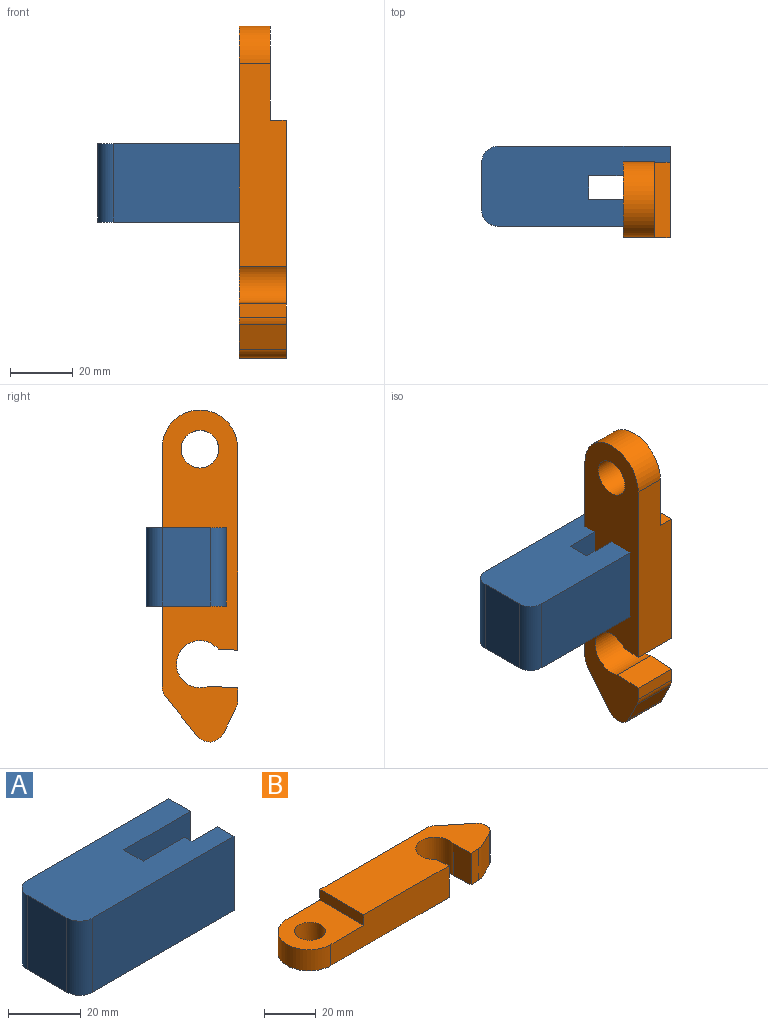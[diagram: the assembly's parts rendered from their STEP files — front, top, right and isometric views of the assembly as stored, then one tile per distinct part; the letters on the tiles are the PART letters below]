
ASSEMBLY  parts=2 mates=1
PART A: 14 faces, bbox 60x25.4x25 mm
  f0: plane 25x8.5mm, normal (1,0,0), area 212.5mm2, adj f1,f7,f8,f9
  f1: plane 55x25mm, normal (0,1,0), area 1375mm2, adj f0,f2,f7,f8
  f2: cylinder r=5mm len=25mm, axis (0,0,-1), area 196.3mm2, adj f1,f3,f7,f8
  f3: plane 25x15.4mm, normal (-1,0,0), area 385mm2, adj f2,f4,f7,f8
  f4: cylinder r=5mm len=25mm, axis (0,0,-1), area 196.3mm2, adj f3,f5,f7,f8
  f5: plane 55x25mm, normal (0,-1,0), area 1375mm2, adj f4,f6,f7,f8
  f6: plane 25x6.5mm, normal (1,0,0), area 162.5mm2, adj f5,f7,f8,f13
  f7: plane 60x25.4mm, normal (0,0,1), area 1289.1mm2, adj f0,f1,f2,f3,f4,f5,f6,f9
  f8: plane 60x25.4mm, normal (0,0,-1), area 1289.1mm2, adj f0,f1,f2,f3,f4,f5,f6,f9
  f9: plane 26x25mm, normal (0,-1,0), area 650mm2, adj f0,f7,f8,f10
  f10: plane 25x7.54mm, normal (1,0,0), area 188.5mm2, adj f7,f8,f9,f11
  f11: plane 25x16.18mm, normal (0,1,0), area 404.5mm2, adj f7,f8,f10,f12
  f12: plane 25x2.86mm, normal (1,0,0), area 71.5mm2, adj f7,f8,f11,f13
  f13: plane 25x9.82mm, normal (0,1,0), area 245.5mm2, adj f6,f7,f8,f12
PART B: 17 faces, bbox 105.8x24x15 mm
  f0: plane 15x6.21mm, normal (1,0.06,0), area 93.4mm2, adj f1,f11,f13,f14
  f1: cylinder r=7.5mm len=15mm, axis (0,0,-1), area 492.6mm2, adj f0,f2,f13,f14
  f2: plane 15x9.27mm, normal (-1,-0.06,0), area 139.2mm2, adj f1,f3,f13,f14
  f3: plane 15x4.29mm, normal (0,-1,0), area 64.4mm2, adj f2,f4,f13,f14
  f4: cylinder r=5mm len=15mm, axis (0,0,-1), area 34.4mm2, adj f3,f5,f13,f14
  f5: plane 15x7.93mm, normal (0.44,-0.9,0), area 132.7mm2, adj f4,f6,f13,f14
  f6: cylinder r=5mm len=15mm, axis (0,0,-1), area 150.4mm2, adj f5,f7,f13,f14
  f7: plane 15x12.53mm, normal (0.63,0.78,0), area 241.2mm2, adj f6,f8,f13,f14
  f8: cylinder r=5mm len=15mm, axis (0,0,-1), area 50.8mm2, adj f7,f9,f13,f14
  f9: plane 76.24x15mm, normal (0,1,0), area 1053.6mm2, adj f8,f10,f13,f14,f15,f16
  f10: cylinder r=12mm len=24mm, axis (0,0,-1), area 377mm2, adj f9,f11,f14,f15
  f11: plane 64.52x15mm, normal (0,-1,0), area 877.8mm2, adj f0,f10,f13,f14,f15,f16
  f12: cylinder r=5.99mm len=11.98mm, axis (0,0,-1), area 376.4mm2, adj f14,f15
  f13: plane 75.76x24mm, normal (0,0,1), area 1438.5mm2, adj f0,f1,f2,f3,f4,f5,f6,f7
  f14: plane 105.76x24mm, normal (0,0,-1), area 1984mm2, adj f0,f1,f2,f3,f4,f5,f6,f7
  f15: plane 30x24mm, normal (0,0,1), area 545.5mm2, adj f9,f10,f11,f12,f16
  f16: plane 24x5mm, normal (-1,0,0), area 120mm2, adj f9,f11,f13,f15
PLACE A rot(axis=(1,0,0),180deg) t=(-14.6,19.03,21.06)mm
PLACE B rot(axis=(0,1,0),90deg) t=(30.4,-10,58.51)mm
MATE planar A.f0 <-> B.f13  axis (1,0,0) through (45.4,2.13,-3.94)mm
